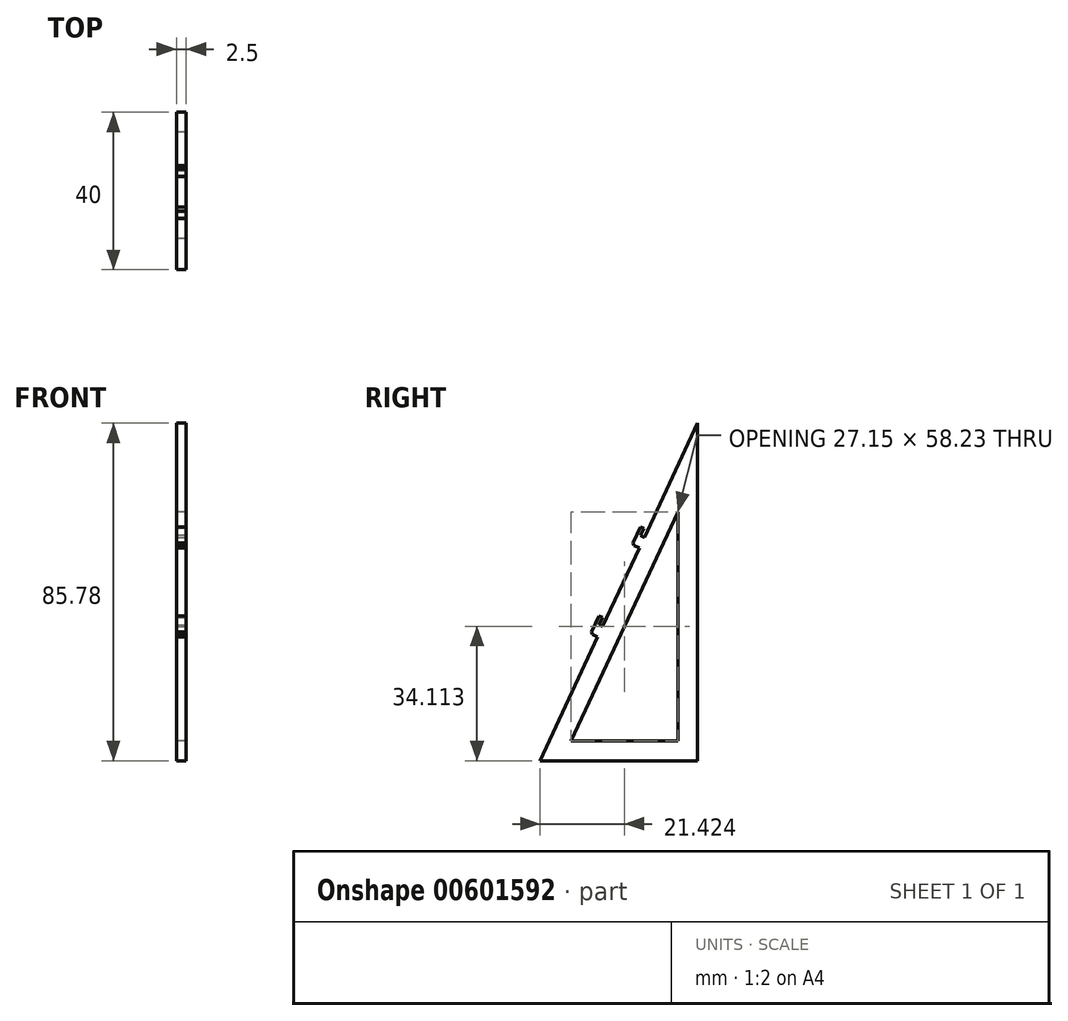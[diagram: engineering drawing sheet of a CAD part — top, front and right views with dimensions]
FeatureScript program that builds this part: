
annotation { "Feature Type Name" : "Feature", "Feature Type Description" : "" }
export const myFeature = defineFeature(function(context is Context, id is Id, definition is map)
    precondition{}
    {
        {
            var Q0;
            Q0=qCreatedBy(makeId("Top.planeOp"),FACE);
            var sketch = newSketch(context, id + "F0", { "sketchPlane" : qUnion([Q0])});
            skLineSegment(sketch, "E0.bottom", {"start": v(0, 0) * mm, "end": v(5, 0) * mm});
            skLineSegment(sketch, "E0.top", {"start": v(0, 40) * mm, "end": v(5, 40) * mm});
            skLineSegment(sketch, "E0.left", {"start": v(0, 0) * mm, "end": v(0, 40) * mm});
            skLineSegment(sketch, "E0.right", {"start": v(5, 0) * mm, "end": v(5, 40) * mm});
            skSolve(sketch);
        }
        {
            var Q0;
            Q0=qCreatedBy(makeId("Right.planeOp"),FACE);
            var sketch = newSketch(context, id + "F1", { "sketchPlane" : qUnion([Q0])});
            skLineSegment(sketch, "E1", {"start": v(40, 0) * mm, "end": v(40, 85.78) * mm});
            skLineSegment(sketch, "E2", {"start": v(0, 0) * mm, "end": v(40, 85.78) * mm});
            skLineSegment(sketch, "E3", {"start": v(0, 0) * mm, "end": v(40, 0) * mm});
            skLineSegment(sketch, "E4.0", {"start": v(7.85, 5) * mm, "end": v(35, 63.23) * mm});
            skLineSegment(sketch, "E4.1", {"start": v(7.85, 5) * mm, "end": v(35, 5) * mm});
            skLineSegment(sketch, "E4.2", {"start": v(35, 5) * mm, "end": v(35, 63.23) * mm});
            skSolve(sketch);
        }
        {
            var Q0;
            Q0=makeQuery(id+"F1.imprint","IMPRINT",FACE,{"disambiguationData":[TD([[makeQuery(id+"F1.imprint","IMPRINT",EDGE,{"derivedFrom":sQuery(id+"F1.wireOp",EDGE,"E1")}),1.0]])]});
            extrude(context, id + "F2", {"entities" : qUnion([Q0]), "depth" : 2.5 * mm, "offsetDistance" : 25 * mm});
        }
        {
            var Q0;
            Q0=makeQuery(id+"F2.opExtrude","SWEPT_FACE",FACE,{"disambiguationData":[OSD([sQuery(id+"F1.wireOp",EDGE,"E2")])]});
            var sketch = newSketch(context, id + "F3", { "sketchPlane" : qUnion([Q0])});
            skLineSegment(sketch, "E5.bottom", {"start": v(0, 64.65) * mm, "end": v(2.5, 64.65) * mm});
            skLineSegment(sketch, "E5.top", {"start": v(0, 59.65) * mm, "end": v(2.5, 59.65) * mm});
            skLineSegment(sketch, "E5.left", {"start": v(0, 64.65) * mm, "end": v(0, 59.65) * mm});
            skLineSegment(sketch, "E5.right", {"start": v(2.5, 64.65) * mm, "end": v(2.5, 59.65) * mm});
            skLineSegment(sketch, "E6.bottom", {"start": v(0, 39.65) * mm, "end": v(2.5, 39.65) * mm});
            skLineSegment(sketch, "E6.top", {"start": v(0, 34.65) * mm, "end": v(2.5, 34.65) * mm});
            skLineSegment(sketch, "E6.left", {"start": v(0, 39.65) * mm, "end": v(0, 34.65) * mm});
            skLineSegment(sketch, "E6.right", {"start": v(2.5, 39.65) * mm, "end": v(2.5, 34.65) * mm});
            skSolve(sketch);
        }
        {
            var Q0;
            Q0=makeQuery(id+"F3.imprint","IMPRINT",FACE,{"disambiguationData":[TD([[makeQuery(id+"F3.imprint","IMPRINT",EDGE,{"derivedFrom":sQuery(id+"F3.wireOp",EDGE,"E5.bottom")}),-1.0]])]});
            var Q1;
            Q1=makeQuery(id+"F3.imprint","IMPRINT",FACE,{"disambiguationData":[TD([[makeQuery(id+"F3.imprint","IMPRINT",EDGE,{"derivedFrom":sQuery(id+"F3.wireOp",EDGE,"E6.bottom")}),-1.0]])]});
            extrude(context, id + "F4", {"entities" : qUnion([Q0, Q1]), "operationType" : NewBodyOperationType.ADD, "depth" : 2 * mm, "offsetDistance" : 25 * mm});
        }
        {
            var Q0;
            Q0=makeQuery(id+"F4.opExtrude","SWEPT_FACE",FACE,{"disambiguationData":[OSD([sQuery(id+"F3.wireOp",EDGE,"E5.bottom")])]});
            var sketch = newSketch(context, id + "F5", { "sketchPlane" : qUnion([Q0])});
            skLineSegment(sketch, "E7.bottom", {"start": v(2.5, 0) * mm, "end": v(0, 0) * mm});
            skLineSegment(sketch, "E7.top", {"start": v(2.5, -1) * mm, "end": v(0, -1) * mm});
            skLineSegment(sketch, "E7.left", {"start": v(2.5, 0) * mm, "end": v(2.5, -1) * mm});
            skLineSegment(sketch, "E7.right", {"start": v(0, 0) * mm, "end": v(0, -1) * mm});
            skSolve(sketch);
        }
        {
            var Q0;
            Q0=makeQuery(id+"F4.opExtrude","SWEPT_FACE",FACE,{"disambiguationData":[OSD([sQuery(id+"F3.wireOp",EDGE,"E6.bottom")])]});
            var sketch = newSketch(context, id + "F6", { "sketchPlane" : qUnion([Q0])});
            skLineSegment(sketch, "E8.bottom", {"start": v(0, 0) * mm, "end": v(2.5, 0) * mm});
            skLineSegment(sketch, "E8.top", {"start": v(0, -1) * mm, "end": v(2.5, -1) * mm});
            skLineSegment(sketch, "E8.left", {"start": v(0, 0) * mm, "end": v(0, -1) * mm});
            skLineSegment(sketch, "E8.right", {"start": v(2.5, 0) * mm, "end": v(2.5, -1) * mm});
            skSolve(sketch);
        }
        {
            var Q0;
            Q0=makeQuery(id+"F5.imprint","IMPRINT",FACE,{"disambiguationData":[TD([[makeQuery(id+"F5.imprint","IMPRINT",EDGE,{"derivedFrom":sQuery(id+"F5.wireOp",EDGE,"E7.bottom")}),-1.0]])]});
            var Q1;
            Q1=makeQuery(id+"F6.imprint","IMPRINT",FACE,{"disambiguationData":[TD([[makeQuery(id+"F6.imprint","IMPRINT",EDGE,{"derivedFrom":sQuery(id+"F6.wireOp",EDGE,"E8.bottom")}),-1.0]])]});
            extrude(context, id + "F7", {"entities" : qUnion([Q0, Q1]), "operationType" : NewBodyOperationType.REMOVE, "oppositeDirection" : true, "depth" : 2 * mm, "offsetDistance" : 25 * mm});
        }
        {
            var Q0;
            Q0=makeQuery(id+"F4.opExtrude","CAP_EDGE",EDGE,{"disambiguationData":[OSD([sQuery(id+"F3.wireOp",EDGE,"E6.top")])],"isStart":false});
            var Q1;
            Q1=makeQuery(id+"F4.opExtrude","CAP_EDGE",EDGE,{"disambiguationData":[OSD([sQuery(id+"F3.wireOp",EDGE,"E5.top")])],"isStart":false});
            chamfer(context, id + "F8", {"entities" : qUnion([Q0, Q1]), "width" : 0.5 * mm, "tangentPropagation" : true});
        }
    });
